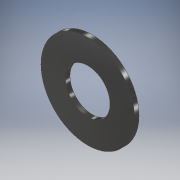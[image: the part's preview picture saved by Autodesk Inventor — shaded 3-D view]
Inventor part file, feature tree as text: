
AUTODESK INVENTOR PART (.ipt)
format: ipt  version: 2018 (Build 220112000, 112)  size: 101,376 bytes
history: native  units: mm
features: extrude x1, sketch x1
ambient origin geometry x8: Origin, YZ Plane, XZ Plane, XY Plane, X Axis, Y Axis, Z Axis, Center Point
bodies: 实体1 (feature_tree)
feature tree (2):
  extrude  "拉伸1"  Depth=2.0mm
  sketch  "草图1"  dims[d0=20.0mm d1=42.0mm d2=2.0mm d3=0.0mm]
